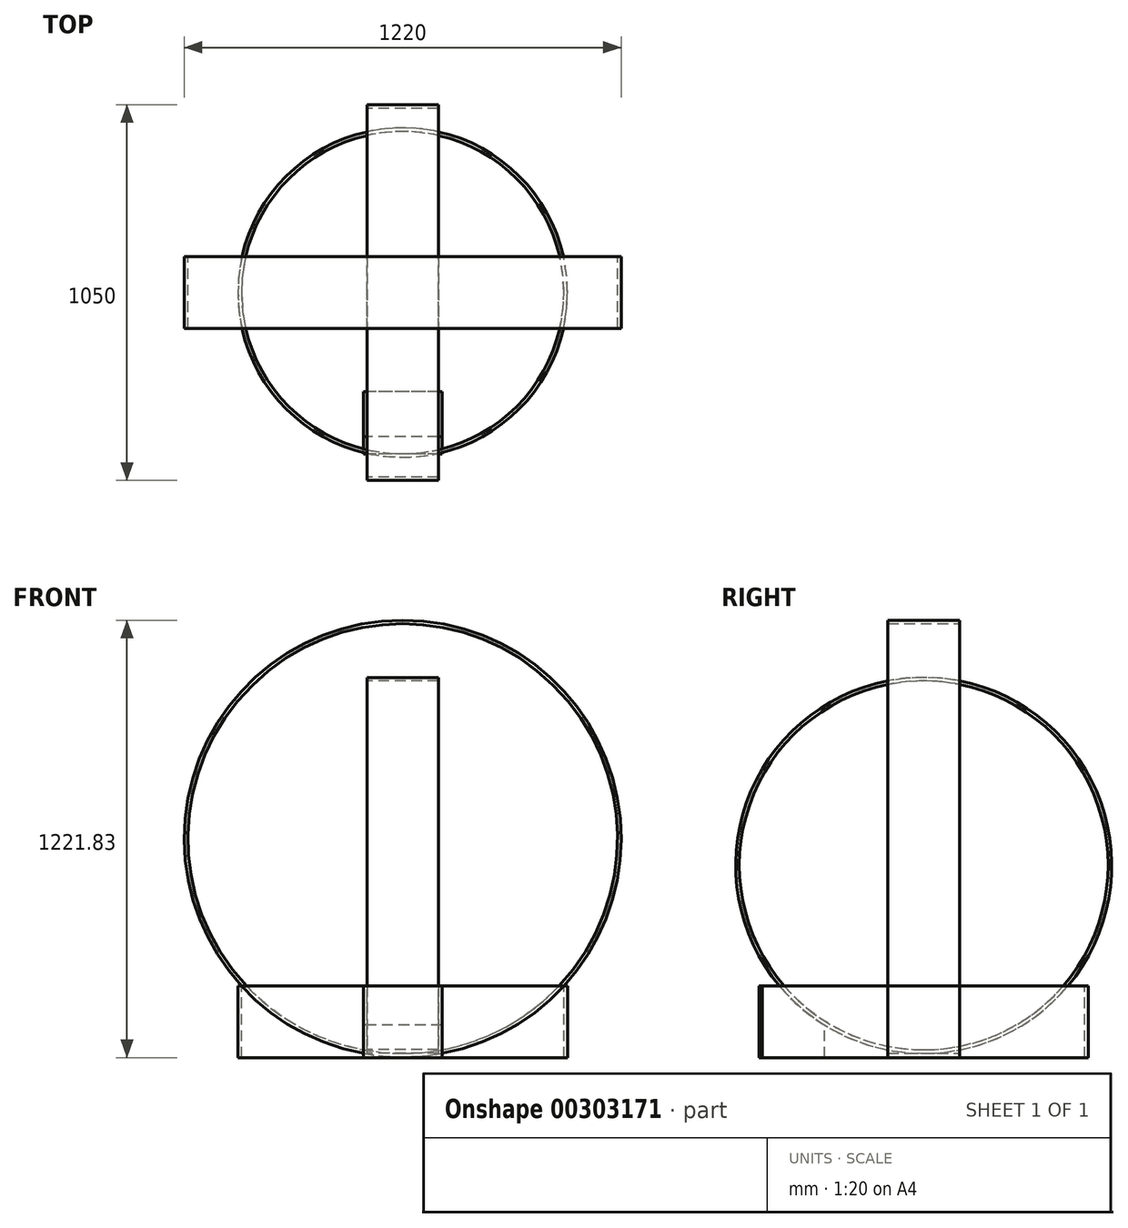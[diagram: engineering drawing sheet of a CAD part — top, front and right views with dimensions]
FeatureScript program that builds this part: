
annotation { "Feature Type Name" : "Feature", "Feature Type Description" : "" }
export const myFeature = defineFeature(function(context is Context, id is Id, definition is map)
    precondition{}
    {
        {
            var Q0;
            Q0=qCreatedBy(makeId("Front.planeOp"),FACE);
            var sketch = newSketch(context, id + "F0", { "sketchPlane" : qUnion([Q0])});
            skLineSegment(sketch, "E0", {"start": v(0, 327) * mm, "end": v(0, -161.17) * mm, "construction": true});
            skLineSegment(sketch, "E1.bottom", {"start": v(-450, 0) * mm, "end": v(-460, 0) * mm});
            skLineSegment(sketch, "E1.top", {"start": v(-450, 200) * mm, "end": v(-460, 200) * mm});
            skLineSegment(sketch, "E1.left", {"start": v(-450, 0) * mm, "end": v(-450, 200) * mm});
            skLineSegment(sketch, "E1.right", {"start": v(-460, 0) * mm, "end": v(-460, 200) * mm});
            skLineSegment(sketch, "E2.MirrorCS", {"start": v(450, 0) * mm, "end": v(460, 0) * mm});
            skLineSegment(sketch, "E3.MirrorCS", {"start": v(450, 200) * mm, "end": v(460, 200) * mm});
            skLineSegment(sketch, "E4.MirrorCS", {"start": v(460, 0) * mm, "end": v(460, 200) * mm});
            skLineSegment(sketch, "E5.MirrorCS", {"start": v(450, 0) * mm, "end": v(450, 200) * mm});
            skCircle(sketch, "E6", {"center": v(0, 611.83) * mm, "radius": 610 * mm});
            skPoint(sketch, "E6.third.point", {"position": v(0, 1221.83) * mm});
            skLineSegment(sketch, "E7", {"start": v(-594.35, 0) * mm, "end": v(638.3, 3.78) * mm, "construction": true});
            skCircle(sketch, "E8", {"center": v(0, 611.83) * mm, "radius": 600 * mm});
            skSolve(sketch);
        }
        {
            var Q0;
            Q0=makeQuery(id+"F0.imprint","IMPRINT",FACE,{"disambiguationData":[TD([[makeQuery(id+"F0.imprint","IMPRINT",EDGE,{"derivedFrom":sQuery(id+"F0.wireOp",EDGE,"E8")}),-1.0]])]});
            extrude(context, id + "F1", {"entities" : qUnion([Q0]), "endBound" : BoundingType.SYMMETRIC, "depth" : 200 * mm});
        }
        {
            var Q0;
            Q0=qCreatedBy(makeId("Front.planeOp"),FACE);
            var sketch = newSketch(context, id + "F2", { "sketchPlane" : qUnion([Q0])});
            skLineSegment(sketch, "E9.0", {"start": v(-460, 0) * mm, "end": v(-460, 200) * mm});
            skLineSegment(sketch, "E9.1", {"start": v(-450, 0) * mm, "end": v(-450, 200) * mm});
            skLineSegment(sketch, "E9.2", {"start": v(-450, 0) * mm, "end": v(-460, 0) * mm});
            skLineSegment(sketch, "E9.3", {"start": v(-450, 200) * mm, "end": v(-460, 200) * mm});
            skLineSegment(sketch, "E10.0", {"start": v(0, 327) * mm, "end": v(0, -161.17) * mm});
            skSolve(sketch);
        }
        {
            var Q0;
            Q0=makeQuery(id+"F0.imprint","IMPRINT",FACE,{"disambiguationData":[TD([[makeQuery(id+"F0.imprint","IMPRINT",EDGE,{"derivedFrom":sQuery(id+"F0.wireOp",EDGE,"E1.bottom")}),-1.0]])]});
            var Q1;
            Q1=sQuery(id+"F2.wireOp",EDGE,"E10.0");
            revolve(context, id + "F3", {"entities" : qUnion([Q0]), "axis" : qUnion([Q1]), "revolveType" : RevolveType.FULL});
        }
        {
            var Q0;
            Q0=qCreatedBy(makeId("Right.planeOp"),FACE);
            var sketch = newSketch(context, id + "F4", { "sketchPlane" : qUnion([Q0])});
            skLineSegment(sketch, "E11", {"start": v(50, 11.83) * mm, "end": v(-50, 11.83) * mm});
            skPoint(sketch, "E12", {"position": v(0, 11.83) * mm});
            skCircle(sketch, "E13", {"center": v(0, 536.83) * mm, "radius": 525 * mm});
            skCircle(sketch, "E14", {"center": v(0, 536.83) * mm, "radius": 515 * mm});
            skSolve(sketch);
        }
        {
            var Q0;
            Q0=makeQuery(id+"F4.imprint","IMPRINT",FACE,{"disambiguationData":[TD([[makeQuery(id+"F4.imprint","IMPRINT",EDGE,{"derivedFrom":sQuery(id+"F4.wireOp",EDGE,"E13")}),1.0]])]});
            extrude(context, id + "F5", {"entities" : qUnion([Q0]), "endBound" : BoundingType.SYMMETRIC, "depth" : 200 * mm});
        }
        {
            var Q0;
            Q0=qCreatedBy(makeId("Right.planeOp"),FACE);
            var sketch = newSketch(context, id + "F6", { "sketchPlane" : qUnion([Q0])});
            skCircle(sketch, "E15.0", {"center": v(0, 536.83) * mm, "radius": 525 * mm});
            skLineSegment(sketch, "E16", {"start": v(-450.37, 199.52) * mm, "end": v(-450.37, 0) * mm});
            skLineSegment(sketch, "E17", {"start": v(-450.37, 0) * mm, "end": v(-276.51, 0) * mm});
            skLineSegment(sketch, "E18", {"start": v(-276.51, 0) * mm, "end": v(-276.51, 90.54) * mm});
            skLineSegment(sketch, "E19", {"start": v(-450.37, 199.52) * mm, "end": v(-402.3, 199.52) * mm});
            skArc(sketch, "E20", {"start": v(-402.3, 199.52) * mm, "mid": v(-343.97, 139.76) * mm, "end": v(-276.51, 90.54) * mm});
            skSolve(sketch);
        }
        {
            var Q0;
            Q0=makeQuery(id+"F6.imprint","IMPRINT",FACE,{"disambiguationData":[TD([[makeQuery(id+"F6.imprint","IMPRINT",EDGE,{"derivedFrom":sQuery(id+"F6.wireOp",EDGE,"E16")}),1.0]])]});
            extrude(context, id + "F7", {"entities" : qUnion([Q0]), "endBound" : BoundingType.SYMMETRIC, "depth" : 220 * mm});
        }
    });
